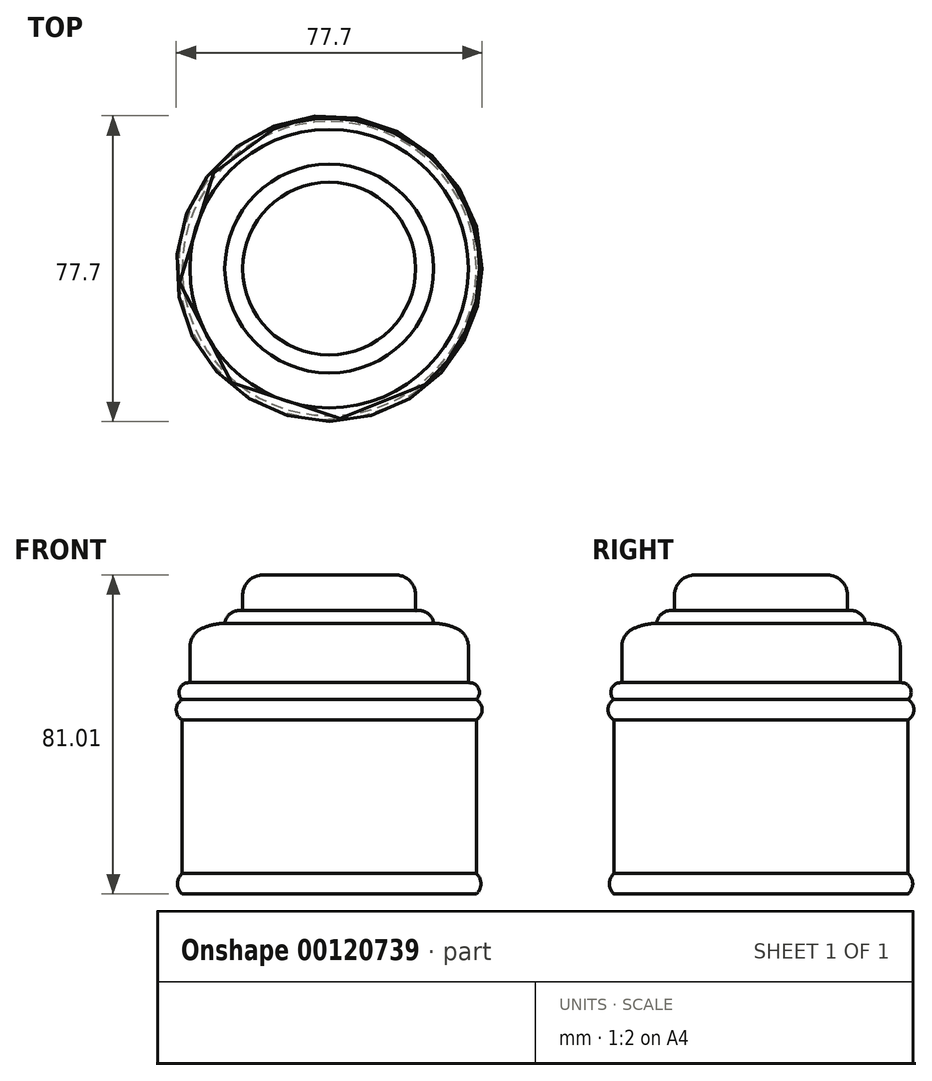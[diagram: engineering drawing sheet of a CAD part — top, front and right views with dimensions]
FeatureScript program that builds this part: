
annotation { "Feature Type Name" : "Feature", "Feature Type Description" : "" }
export const myFeature = defineFeature(function(context is Context, id is Id, definition is map)
    precondition{}
    {
        {
            var Q0;
            Q0=qCreatedBy(makeId("Front.planeOp"),FACE);
            var sketch = newSketch(context, id + "F0", { "sketchPlane" : qUnion([Q0])});
            skLineSegment(sketch, "E0", {"start": v(0, 45.78) * mm, "end": v(21.96, 45.78) * mm});
            skLineSegment(sketch, "E1", {"start": v(21.96, 45.78) * mm, "end": v(21.96, 36.65) * mm});
            skArc(sketch, "E2", {"start": v(26.53, 33.52) * mm, "mid": v(24.95, 36.12) * mm, "end": v(21.96, 36.65) * mm});
            skArc(sketch, "E3", {"start": v(35.37, 30.38) * mm, "mid": v(31.2, 32.65) * mm, "end": v(26.53, 33.52) * mm});
            skLineSegment(sketch, "E4", {"start": v(35.37, 30.38) * mm, "end": v(35.37, 18.4) * mm});
            skArc(sketch, "E5", {"start": v(37.37, 14.12) * mm, "mid": v(37.93, 16.99) * mm, "end": v(35.37, 18.4) * mm});
            skArc(sketch, "E6", {"start": v(37.37, 8.99) * mm, "mid": v(38.85, 11.55) * mm, "end": v(37.37, 14.12) * mm});
            skLineSegment(sketch, "E7", {"start": v(37.37, 8.99) * mm, "end": v(37.37, -30.1) * mm});
            skArc(sketch, "E8", {"start": v(37.37, -35.23) * mm, "mid": v(38.54, -32.66) * mm, "end": v(37.37, -30.1) * mm});
            skLineSegment(sketch, "E9", {"start": v(37.37, -35.23) * mm, "end": v(0, -35.23) * mm});
            skLineSegment(sketch, "E10", {"start": v(0, 45.78) * mm, "end": v(0, -35.23) * mm});
            skSolve(sketch);
        }
        {
            var Q0;
            Q0=makeQuery(id+"F0.imprint","IMPRINT",FACE,{"disambiguationData":[TD([[makeQuery(id+"F0.imprint","IMPRINT",EDGE,{"derivedFrom":sQuery(id+"F0.wireOp",EDGE,"E0")}),-1.0]])]});
            var Q1;
            Q1=sQuery(id+"F0.wireOp",EDGE,"E10");
            revolve(context, id + "F1", {"entities" : qUnion([Q0]), "axis" : qUnion([Q1]), "revolveType" : RevolveType.FULL});
        }
        {
            var Q0;
            Q0=makeQuery(id+"F1.opRevolve","SWEPT_EDGE",EDGE,{"disambiguationData":[OSD([sQuery(id+"F0.wireOp",EDGE,"E0"),sQuery(id+"F0.wireOp",EDGE,"E1")])]});
            var Q1;
            Q1=makeQuery(id+"F1.opRevolve","SWEPT_EDGE",EDGE,{"disambiguationData":[OSD([sQuery(id+"F0.wireOp",EDGE,"E3"),sQuery(id+"F0.wireOp",EDGE,"E4")])]});
            fillet(context, id + "F2", {"entities" : qUnion([Q0, Q1]), "radius" : 5.08 * mm, "tangentPropagation" : true, "allowEdgeOverflow" : false});
        }
    });
